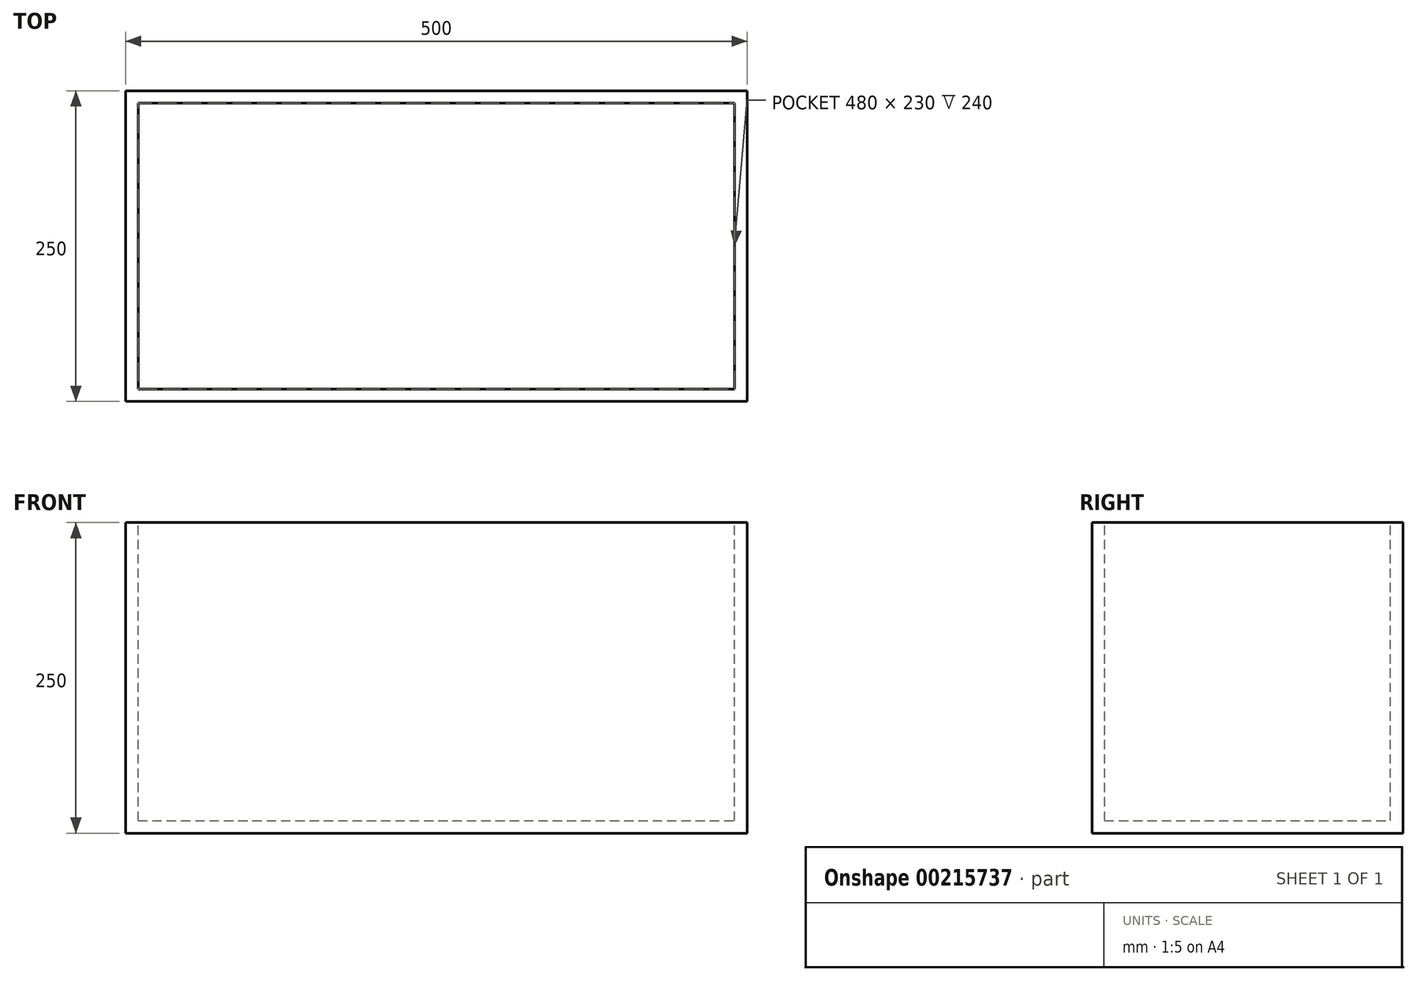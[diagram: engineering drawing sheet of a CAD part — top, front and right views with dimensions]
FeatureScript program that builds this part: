
annotation { "Feature Type Name" : "Feature", "Feature Type Description" : "" }
export const myFeature = defineFeature(function(context is Context, id is Id, definition is map)
    precondition{}
    {
        {
            var Q0;
            Q0=qCreatedBy(makeId("Top.planeOp"),FACE);
            var sketch = newSketch(context, id + "F0", { "sketchPlane" : qUnion([Q0])});
            skLineSegment(sketch, "E0.bottom", {"start": v(0, 0) * mm, "end": v(500, 0) * mm});
            skLineSegment(sketch, "E0.top", {"start": v(0, 250) * mm, "end": v(500, 250) * mm});
            skLineSegment(sketch, "E0.left", {"start": v(0, 0) * mm, "end": v(0, 250) * mm});
            skLineSegment(sketch, "E0.right", {"start": v(500, 0) * mm, "end": v(500, 250) * mm});
            skSolve(sketch);
        }
        {
            var Q0;
            Q0 = qSketchRegion(id + "F0", true);
            extrude(context, id + "F1", {"entities" : qUnion([Q0]), "oppositeDirection" : true, "depth" : 250 * mm});
        }
        {
            var Q0;
            Q0=qCreatedBy(makeId("Top.planeOp"),FACE);
            var sketch = newSketch(context, id + "F2", { "sketchPlane" : qUnion([Q0])});
            skLineSegment(sketch, "E1.bottom", {"start": v(10, 10) * mm, "end": v(490, 10) * mm});
            skLineSegment(sketch, "E1.top", {"start": v(10, 240) * mm, "end": v(490, 240) * mm});
            skLineSegment(sketch, "E1.left", {"start": v(10, 10) * mm, "end": v(10, 240) * mm});
            skLineSegment(sketch, "E1.right", {"start": v(490, 10) * mm, "end": v(490, 240) * mm});
            skSolve(sketch);
        }
        {
            var Q0;
            Q0 = qSketchRegion(id + "F2", true);
            extrude(context, id + "F3", {"entities" : qUnion([Q0]), "operationType" : NewBodyOperationType.REMOVE, "oppositeDirection" : true, "depth" : 240 * mm});
        }
    });
